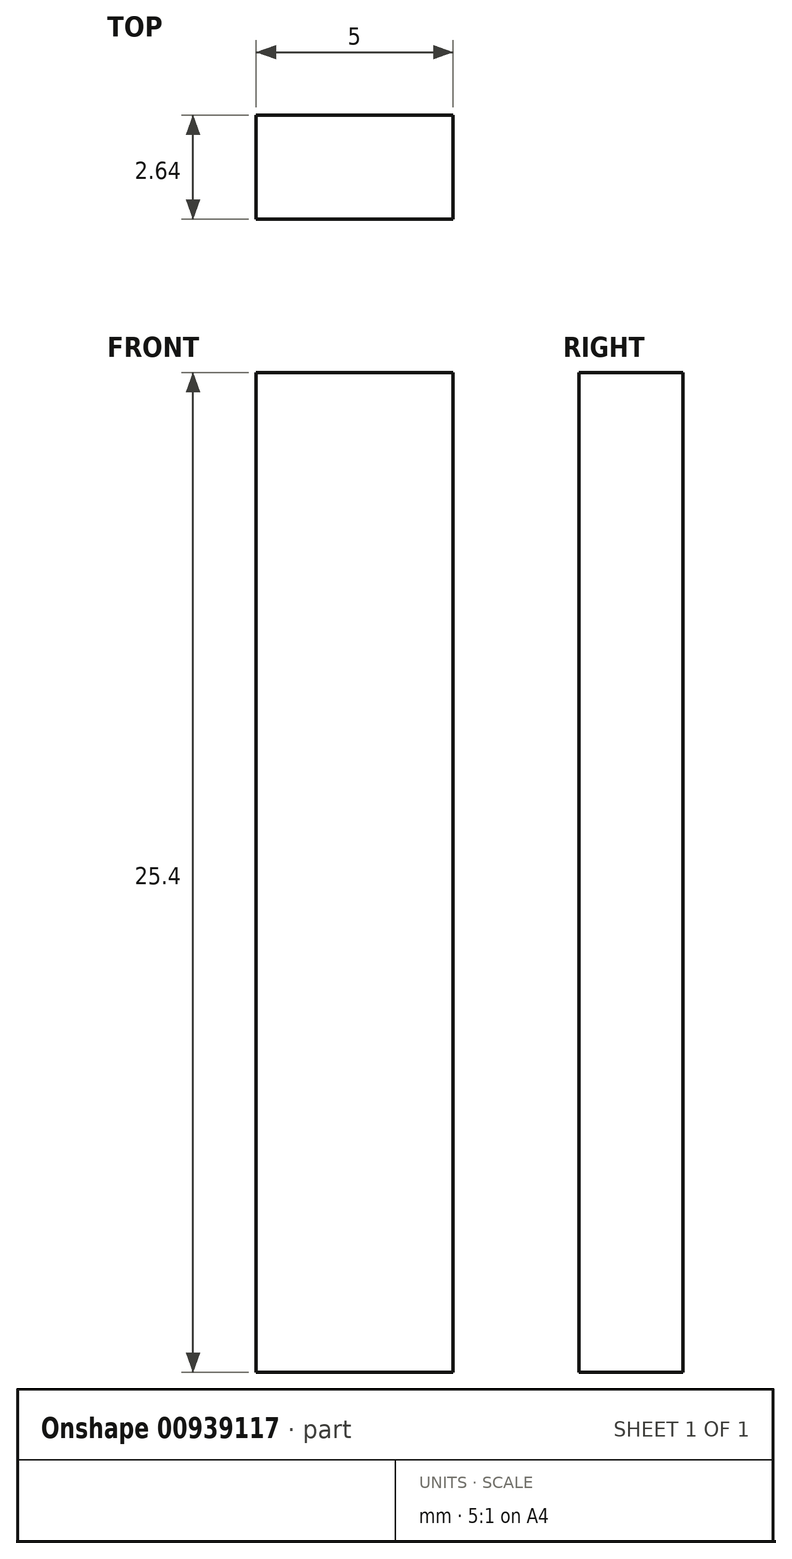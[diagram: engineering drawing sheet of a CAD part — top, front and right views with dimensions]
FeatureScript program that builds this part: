
annotation { "Feature Type Name" : "Feature", "Feature Type Description" : "" }
export const myFeature = defineFeature(function(context is Context, id is Id, definition is map)
    precondition{}
    {
        {
            var Q0;
            Q0=qCreatedBy(makeId("Top.planeOp"),FACE);
            var sketch = newSketch(context, id + "F0", { "sketchPlane" : qUnion([Q0])});
            skLineSegment(sketch, "E0.bottom", {"start": v(2.5, 1.32) * mm, "end": v(-2.5, 1.32) * mm});
            skLineSegment(sketch, "E0.top", {"start": v(2.5, -1.32) * mm, "end": v(-2.5, -1.32) * mm});
            skLineSegment(sketch, "E0.left", {"start": v(2.5, 1.32) * mm, "end": v(2.5, -1.32) * mm});
            skLineSegment(sketch, "E0.right", {"start": v(-2.5, 1.32) * mm, "end": v(-2.5, -1.32) * mm});
            skPoint(sketch, "E0.middle", {"position": v(0, 0) * mm});
            skSolve(sketch);
        }
        {
            var Q0;
            Q0 = qSketchRegion(id + "F0", true);
            extrude(context, id + "F1", {"entities" : qUnion([Q0]), "depth" : 25.4 * mm, "offsetDistance" : 25.4 * mm});
        }
    });
